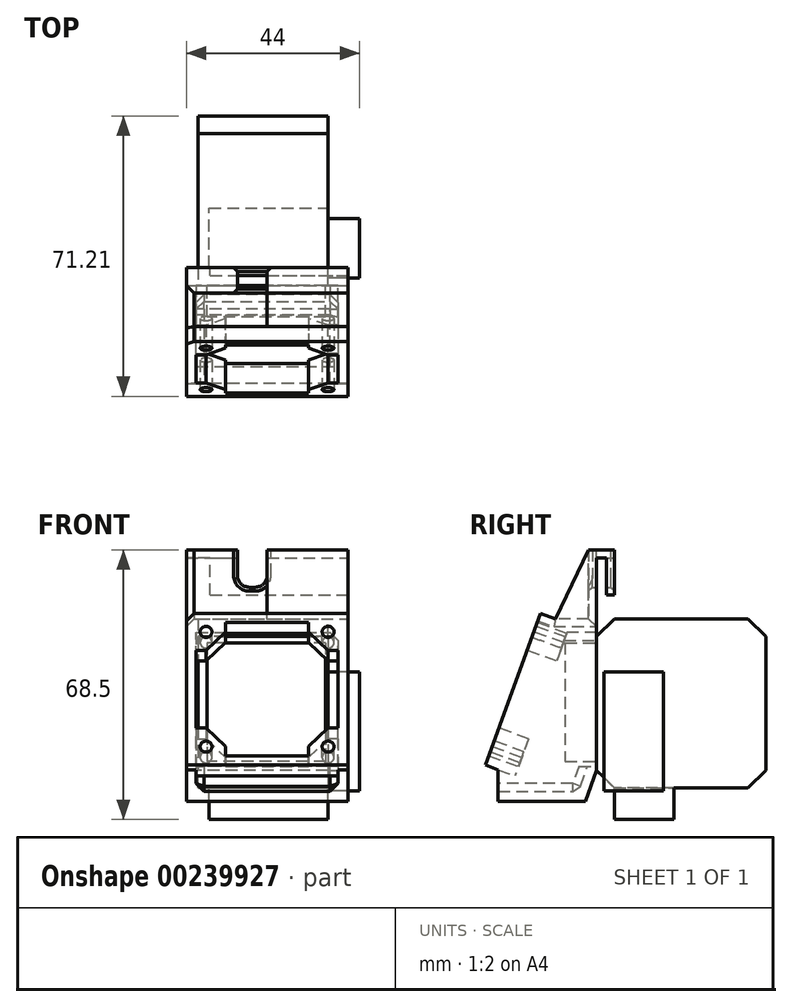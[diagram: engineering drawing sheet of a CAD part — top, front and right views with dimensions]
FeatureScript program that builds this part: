
annotation { "Feature Type Name" : "Feature", "Feature Type Description" : "" }
export const myFeature = defineFeature(function(context is Context, id is Id, definition is map)
    precondition{}
    {
        {
            var Q0;
            Q0=qCreatedBy(makeId("Front.planeOp"),FACE);
            var sketch = newSketch(context, id + "F0", { "sketchPlane" : qUnion([Q0])});
            skLineSegment(sketch, "E0.bottom", {"start": v(0, 0) * mm, "end": v(-33, 0) * mm});
            skLineSegment(sketch, "E0.top", {"start": v(0, -43) * mm, "end": v(-33, -43) * mm});
            skLineSegment(sketch, "E0.left", {"start": v(0, 0) * mm, "end": v(0, -43) * mm});
            skLineSegment(sketch, "E0.right", {"start": v(-33, 0) * mm, "end": v(-33, -43) * mm});
            skSolve(sketch);
        }
        {
            var Q0;
            Q0=makeQuery(id+"F0.imprint","IMPRINT",FACE,{"disambiguationData":[TD([[makeQuery(id+"F0.imprint","IMPRINT",EDGE,{"derivedFrom":sQuery(id+"F0.wireOp",EDGE,"E0.bottom")}),1.0]])]});
            extrude(context, id + "F1", {"entities" : qUnion([Q0]), "oppositeDirection" : true, "depth" : 43 * mm, "offsetDistance" : 25 * mm});
        }
        {
            var Q0;
            Q0=makeQuery(id+"F1.opExtrude","CAP_EDGE",EDGE,{"disambiguationData":[OSD([sQuery(id+"F0.wireOp",EDGE,"E0.bottom")])],"isStart":true});
            var Q1;
            Q1=makeQuery(id+"F1.opExtrude","CAP_EDGE",EDGE,{"disambiguationData":[OSD([sQuery(id+"F0.wireOp",EDGE,"E0.bottom")])],"isStart":false});
            var Q2;
            Q2=makeQuery(id+"F1.opExtrude","CAP_EDGE",EDGE,{"disambiguationData":[OSD([sQuery(id+"F0.wireOp",EDGE,"E0.top")])],"isStart":true});
            var Q3;
            Q3=makeQuery(id+"F1.opExtrude","CAP_EDGE",EDGE,{"disambiguationData":[OSD([sQuery(id+"F0.wireOp",EDGE,"E0.top")])],"isStart":false});
            chamfer(context, id + "F2", {"entities" : qUnion([Q0, Q1, Q2, Q3]), "width" : 4.5 * mm, "tangentPropagation" : true});
        }
        {
            var Q0;
            Q0=makeQuery(id+"F1.opExtrude","CAP_FACE",FACE,{"disambiguationData":[OSD([sQuery(id+"F0.wireOp",EDGE,"E0.bottom"),sQuery(id+"F0.wireOp",EDGE,"E0.top"),sQuery(id+"F0.wireOp",EDGE,"E0.left"),sQuery(id+"F0.wireOp",EDGE,"E0.right")])],"isStart":true});
            var sketch = newSketch(context, id + "F3", { "sketchPlane" : qUnion([Q0])});
            skLineSegment(sketch, "E1.bottom", {"start": v(-0.6, -6.1) * mm, "end": v(-30.8, -6.1) * mm});
            skLineSegment(sketch, "E1.top", {"start": v(-0.6, -36.3) * mm, "end": v(-30.8, -36.3) * mm});
            skLineSegment(sketch, "E1.left", {"start": v(-0.6, -6.1) * mm, "end": v(-0.6, -36.3) * mm});
            skLineSegment(sketch, "E1.right", {"start": v(-30.8, -6.1) * mm, "end": v(-30.8, -36.3) * mm});
            skSolve(sketch);
        }
        {
            var Q0;
            Q0 = qSketchRegion(id + "F3", true);
            extrude(context, id + "F4", {"entities" : qUnion([Q0]), "operationType" : NewBodyOperationType.ADD, "depth" : 8 * mm, "offsetDistance" : 25 * mm});
        }
        {
            var Q0;
            Q0=makeQuery(id+"F1.opExtrude","SWEPT_FACE",FACE,{"disambiguationData":[OSD([sQuery(id+"F0.wireOp",EDGE,"E0.top")])]});
            var sketch = newSketch(context, id + "F5", { "sketchPlane" : qUnion([Q0])});
            skLineSegment(sketch, "E2.bottom", {"start": v(-30.2, -4.5) * mm, "end": v(0, -4.5) * mm});
            skLineSegment(sketch, "E2.top", {"start": v(-30.2, -19.6) * mm, "end": v(0, -19.6) * mm});
            skLineSegment(sketch, "E2.left", {"start": v(-30.2, -4.5) * mm, "end": v(-30.2, -19.6) * mm});
            skLineSegment(sketch, "E2.right", {"start": v(0, -4.5) * mm, "end": v(0, -19.6) * mm});
            skSolve(sketch);
        }
        {
            var Q0;
            Q0 = qSketchRegion(id + "F5", true);
            extrude(context, id + "F6", {"entities" : qUnion([Q0]), "operationType" : NewBodyOperationType.ADD, "depth" : 8 * mm, "offsetDistance" : 25 * mm});
        }
        {
            var Q0;
            Q0=makeQuery(id+"F6.boolean.opBoolean","MERGE",FACE,{"derivedFrom":[makeQuery(id+"F1.opExtrude","SWEPT_FACE",FACE,{"disambiguationData":[OSD([sQuery(id+"F0.wireOp",EDGE,"E0.left")])]}),makeQuery(id+"F6.opExtrude","SWEPT_FACE",FACE,{"disambiguationData":[OSD([sQuery(id+"F5.wireOp",EDGE,"E2.right")])]})]});
            var sketch = newSketch(context, id + "F7", { "sketchPlane" : qUnion([Q0])});
            skLineSegment(sketch, "E3.bottom", {"start": v(1.85, -13.5) * mm, "end": v(16.95, -13.5) * mm});
            skLineSegment(sketch, "E3.top", {"start": v(1.85, -43.7) * mm, "end": v(16.95, -43.7) * mm});
            skLineSegment(sketch, "E3.left", {"start": v(1.85, -13.5) * mm, "end": v(1.85, -43.7) * mm});
            skLineSegment(sketch, "E3.right", {"start": v(16.95, -13.5) * mm, "end": v(16.95, -43.7) * mm});
            skSolve(sketch);
        }
        {
            var Q0;
            Q0 = qSketchRegion(id + "F7", true);
            extrude(context, id + "F8", {"entities" : qUnion([Q0]), "operationType" : NewBodyOperationType.ADD, "depth" : 8 * mm, "offsetDistance" : 25 * mm});
        }
        {
            var Q0;
            Q0=qCreatedBy(makeId("Right.planeOp"),FACE);
            cPlane(context, id + "F9", {"entities" : qUnion([Q0]), "cplaneType" : CPlaneType.OFFSET, "offset" : 5 * mm, "width" : 150 * mm, "height" : 150 * mm});
        }
        {
            var Q0;
            Q0=qCreatedBy(id+"F9.planeOp",FACE);
            var sketch = newSketch(context, id + "F10", { "sketchPlane" : qUnion([Q0])});
            skLineSegment(sketch, "E4", {"start": v(-2, -3.5) * mm, "end": v(-2, 17.5) * mm});
            skLineSegment(sketch, "E5", {"start": v(-2, 17.5) * mm, "end": v(4.5, 17.5) * mm});
            skLineSegment(sketch, "E6", {"start": v(4.5, 17.5) * mm, "end": v(4.5, 6) * mm});
            skLineSegment(sketch, "E7", {"start": v(4.5, 6) * mm, "end": v(2.5, 6) * mm});
            skLineSegment(sketch, "E8", {"start": v(2.5, 6) * mm, "end": v(2.5, 15.5) * mm});
            skLineSegment(sketch, "E9", {"start": v(2.5, 15.5) * mm, "end": v(0, 15.5) * mm});
            skLineSegment(sketch, "E10", {"start": v(0, 15.5) * mm, "end": v(0, -3.5) * mm});
            skLineSegment(sketch, "E11", {"start": v(0, -3.5) * mm, "end": v(-2, -3.5) * mm});
            skSolve(sketch);
        }
        {
            var Q0;
            Q0 = qSketchRegion(id + "F10", true);
            extrude(context, id + "F11", {"entities" : qUnion([Q0]), "oppositeDirection" : true, "depth" : 35 * mm, "offsetDistance" : 25 * mm});
        }
        {
            var Q0;
            Q0=makeQuery(id+"F11.opExtrude","SWEPT_FACE",FACE,{"disambiguationData":[OSD([sQuery(id+"F10.wireOp",EDGE,"E4")])]});
            var sketch = newSketch(context, id + "F12", { "sketchPlane" : qUnion([Q0])});
            skLineSegment(sketch, "E12", {"start": v(-15.5, 8) * mm, "end": v(-15.5, 17.5) * mm});
            skLineSegment(sketch, "E13", {"start": v(-15.5, 8) * mm, "end": v(-23, 8) * mm});
            skLineSegment(sketch, "E14", {"start": v(-23, 17.5) * mm, "end": v(-23, 8) * mm});
            skLineSegment(sketch, "E15", {"start": v(-23, 17.5) * mm, "end": v(-15.5, 17.5) * mm});
            skSolve(sketch);
        }
        {
            var Q0;
            Q0 = qSketchRegion(id + "F12", true);
            var Q1;
            Q1=makeQuery(id+"F11.opExtrude","SWEPT_FACE",FACE,{"disambiguationData":[OSD([sQuery(id+"F10.wireOp",EDGE,"E6")])]});
            extrude(context, id + "F13", {"entities" : qUnion([Q0]), "operationType" : NewBodyOperationType.REMOVE, "endBound" : BoundingType.SYMMETRIC, "depth" : 50 * mm, "endBoundEntityFace" : qUnion([Q1]), "offsetDistance" : 25 * mm});
        }
        {
            var Q0;
            {var subQ0=sQuery(id+"F12.wireOp",EDGE,"E13");var subQ1=sQuery(id+"F12.wireOp",EDGE,"E12");Q0=makeQuery(id+"F13.boolean.opBoolean","COPY",EDGE,{"disambiguationData":[TD([makeQuery(id+"F11.opExtrude","SWEPT_FACE",FACE,{"disambiguationData":[OSD([sQuery(id+"F10.wireOp",EDGE,"E6")])]})])],"derivedFrom":makeQuery(id+"F13.opExtrude","SWEPT_EDGE",EDGE,{"disambiguationData":[OSD([subQ1,subQ0])]})});}
            var Q1;
            {var subQ0=sQuery(id+"F12.wireOp",EDGE,"E12");var subQ1=sQuery(id+"F12.wireOp",EDGE,"E13");Q1=makeQuery(id+"F13.boolean.opBoolean","COPY",EDGE,{"disambiguationData":[TD([makeQuery(id+"F11.opExtrude","SWEPT_FACE",FACE,{"disambiguationData":[OSD([sQuery(id+"F10.wireOp",EDGE,"E4")])]})])],"derivedFrom":makeQuery(id+"F13.opExtrude","SWEPT_EDGE",EDGE,{"disambiguationData":[OSD([subQ0,subQ1])]})});}
            var Q2;
            {var subQ0=sQuery(id+"F12.wireOp",EDGE,"E13");var subQ1=sQuery(id+"F12.wireOp",EDGE,"E14");Q2=makeQuery(id+"F13.boolean.opBoolean","COPY",EDGE,{"disambiguationData":[TD([makeQuery(id+"F11.opExtrude","SWEPT_FACE",FACE,{"disambiguationData":[OSD([sQuery(id+"F10.wireOp",EDGE,"E6")])]})])],"derivedFrom":makeQuery(id+"F13.opExtrude","SWEPT_EDGE",EDGE,{"disambiguationData":[OSD([subQ0,subQ1])]})});}
            var Q3;
            {var subQ0=sQuery(id+"F12.wireOp",EDGE,"E13");var subQ1=sQuery(id+"F12.wireOp",EDGE,"E14");Q3=makeQuery(id+"F13.boolean.opBoolean","COPY",EDGE,{"disambiguationData":[TD([makeQuery(id+"F11.opExtrude","SWEPT_FACE",FACE,{"disambiguationData":[OSD([sQuery(id+"F10.wireOp",EDGE,"E4")])]})])],"derivedFrom":makeQuery(id+"F13.opExtrude","SWEPT_EDGE",EDGE,{"disambiguationData":[OSD([subQ0,subQ1])]})});}
            fillet(context, id + "F14", {"entities" : qUnion([Q0, Q1, Q2, Q3]), "radius" : 3 * mm, "tangentPropagation" : true, "allowEdgeOverflow" : false});
        }
        {
            var Q0;
            Q0=qCreatedBy(id+"F9.planeOp",FACE);
            var sketch = newSketch(context, id + "F15", { "sketchPlane" : qUnion([Q0])});
            skLineSegment(sketch, "E16", {"start": v(-10.5, 0) * mm, "end": v(-24.45, -38.55) * mm});
            skLineSegment(sketch, "E17", {"start": v(-24.45, -38.55) * mm, "end": v(-2.85, -46.37) * mm});
            skLineSegment(sketch, "E18", {"start": v(-10.5, 0) * mm, "end": v(-2, 17.5) * mm});
            skPoint(sketch, "E19.orphan", {"position": v(19.6, 0) * mm});
            skLineSegment(sketch, "E20", {"start": v(0, -38.5) * mm, "end": v(0, 17.5) * mm});
            skLineSegment(sketch, "E21", {"start": v(0, 17.5) * mm, "end": v(-2, 17.5) * mm});
            skLineSegment(sketch, "E22", {"start": v(-2.85, -46.37) * mm, "end": v(0, -38.5) * mm});
            skLineSegment(sketch, "E23", {"start": v(-2.85, -46.37) * mm, "end": v(0, -47.4) * mm, "construction": true});
            skLineSegment(sketch, "E24", {"start": v(0, -47.4) * mm, "end": v(0, -38.5) * mm, "construction": true});
            skSolve(sketch);
        }
        {
            var Q0;
            Q0 = qSketchRegion(id + "F15", true);
            var Q1;
            Q1=makeQuery(id+"F6.boolean.opBoolean","MERGE",FACE,{"derivedFrom":[makeQuery(id+"F1.opExtrude","SWEPT_FACE",FACE,{"disambiguationData":[OSD([sQuery(id+"F0.wireOp",EDGE,"E0.left")])]}),makeQuery(id+"F6.opExtrude","SWEPT_FACE",FACE,{"disambiguationData":[OSD([sQuery(id+"F5.wireOp",EDGE,"E2.right")])]})]});
            extrude(context, id + "F16", {"entities" : qUnion([Q0]), "operationType" : NewBodyOperationType.ADD, "oppositeDirection" : true, "depth" : 2.5 * mm, "endBoundEntityFace" : qUnion([Q1]), "offsetDistance" : 25 * mm});
        }
        {
            var Q0;
            Q0=qCreatedBy(id+"F9.planeOp",FACE);
            var sketch = newSketch(context, id + "F17", { "sketchPlane" : qUnion([Q0])});
            skLineSegment(sketch, "E25", {"start": v(0, -3.5) * mm, "end": v(-8.17, -3.5) * mm});
            skLineSegment(sketch, "E26", {"start": v(-11.77, -3.5) * mm, "end": v(-11.35, -2.35) * mm, "construction": true});
            skLineSegment(sketch, "E27", {"start": v(-10.5, 0) * mm, "end": v(-2, 17.5) * mm});
            skLineSegment(sketch, "E28", {"start": v(-2, 17.5) * mm, "end": v(0, 17.5) * mm});
            skLineSegment(sketch, "E29", {"start": v(0, 17.5) * mm, "end": v(0, -3.5) * mm});
            skLineSegment(sketch, "E30", {"start": v(0, 17.5) * mm, "end": v(4.5, 17.5) * mm});
            skLineSegment(sketch, "E31", {"start": v(4.5, 17.5) * mm, "end": v(4.5, 15.5) * mm});
            skLineSegment(sketch, "E32", {"start": v(4.5, 15.5) * mm, "end": v(0, 15.5) * mm});
            skLineSegment(sketch, "E33", {"start": v(-11.35, -2.35) * mm, "end": v(-10.5, 0) * mm});
            skLineSegment(sketch, "E34", {"start": v(-11.35, -2.35) * mm, "end": v(-8.17, -3.5) * mm});
            skSolve(sketch);
        }
        {
            var Q0;
            Q0=makeQuery(id+"F16.opExtrude","SWEPT_FACE",FACE,{"disambiguationData":[OSD([sQuery(id+"F15.wireOp",EDGE,"E16")])]});
            var sketch = newSketch(context, id + "F18", { "sketchPlane" : qUnion([Q0])});
            skLineSegment(sketch, "E35", {"start": v(5, -3.57) * mm, "end": v(-36, -3.57) * mm});
            skLineSegment(sketch, "E36", {"start": v(-36, -3.57) * mm, "end": v(-36, -44.57) * mm});
            skLineSegment(sketch, "E37", {"start": v(-36, -44.57) * mm, "end": v(5, -44.57) * mm});
            skLineSegment(sketch, "E38", {"start": v(5, -44.57) * mm, "end": v(5, -3.57) * mm});
            skLineSegment(sketch, "E39.bottom", {"start": v(-33.5, -6.07) * mm, "end": v(2.5, -6.07) * mm});
            skLineSegment(sketch, "E39.top", {"start": v(-33.5, -42.07) * mm, "end": v(2.5, -42.07) * mm});
            skLineSegment(sketch, "E39.left", {"start": v(-33.5, -6.07) * mm, "end": v(-33.5, -42.07) * mm});
            skLineSegment(sketch, "E39.right", {"start": v(2.5, -6.07) * mm, "end": v(2.5, -42.07) * mm});
            skSolve(sketch);
        }
        {
            var Q0;
            Q0 = qSketchRegion(id + "F18", true);
            extrude(context, id + "F19", {"entities" : qUnion([Q0]), "operationType" : NewBodyOperationType.ADD, "endBound" : BoundingType.SYMMETRIC, "depth" : 8 * mm, "offsetDistance" : 25 * mm});
        }
        {
            var Q0;
            Q0 = qSketchRegion(id + "F17", true);
            var Q1;
            Q1=makeQuery(id+"F13.boolean.opBoolean","COPY",FACE,{"derivedFrom":makeQuery(id+"F13.opExtrude","SWEPT_FACE",FACE,{"disambiguationData":[OSD([sQuery(id+"F12.wireOp",EDGE,"E12")])]})});
            extrude(context, id + "F20", {"entities" : qUnion([Q0]), "operationType" : NewBodyOperationType.ADD, "endBound" : BoundingType.UP_TO_SURFACE, "oppositeDirection" : true, "depth" : 25 * mm, "endBoundEntityFace" : qUnion([Q1]), "offsetDistance" : 25 * mm});
        }
        {
            var Q0;
            Q0=makeQuery(id+"F19.opExtrude","SWEPT_FACE",FACE,{"disambiguationData":[OSD([sQuery(id+"F18.wireOp",EDGE,"E36")])]});
            var sketch = newSketch(context, id + "F21", { "sketchPlane" : qUnion([Q0])});
            skLineSegment(sketch, "E40", {"start": v(0, -3.5) * mm, "end": v(7.51, -3.5) * mm});
            skLineSegment(sketch, "E41", {"start": v(7.51, -3.5) * mm, "end": v(11.27, -2.14) * mm});
            skLineSegment(sketch, "E42", {"start": v(11.27, -2.14) * mm, "end": v(10.5, 0) * mm});
            skLineSegment(sketch, "E43", {"start": v(10.5, 0) * mm, "end": v(0, 0) * mm});
            skLineSegment(sketch, "E44", {"start": v(0, 0) * mm, "end": v(0, -3.5) * mm});
            skSolve(sketch);
        }
        {
            var Q0;
            Q0 = qSketchRegion(id + "F21", true);
            var Q1;
            {var subQ0=sQuery(id+"F12.wireOp",EDGE,"E12");Q1=makeQuery(id+"F20.boolean.opBoolean","MERGE",FACE,{"derivedFrom":[makeQuery(id+"F13.boolean.opBoolean","COPY",FACE,{"derivedFrom":makeQuery(id+"F13.opExtrude","SWEPT_FACE",FACE,{"disambiguationData":[OSD([subQ0])]})}),makeQuery(id+"F20.opExtrude","CAP_FACE",FACE,{"disambiguationData":[OSD([subQ0])],"isStart":false})]});}
            extrude(context, id + "F22", {"entities" : qUnion([Q0]), "operationType" : NewBodyOperationType.ADD, "endBound" : BoundingType.UP_TO_SURFACE, "oppositeDirection" : true, "depth" : 25 * mm, "endBoundEntityFace" : qUnion([Q1]), "offsetDistance" : 25 * mm});
        }
        {
            var Q0;
            Q0=makeQuery(id+"F22.boolean.opBoolean","MERGE",FACE,{"derivedFrom":[makeQuery(id+"F19.opExtrude","SWEPT_FACE",FACE,{"disambiguationData":[OSD([sQuery(id+"F18.wireOp",EDGE,"E36")])]}),makeQuery(id+"F22.opExtrude","CAP_FACE",FACE,{"disambiguationData":[OSD([sQuery(id+"F21.wireOp",EDGE,"E40"),sQuery(id+"F21.wireOp",EDGE,"E41"),sQuery(id+"F21.wireOp",EDGE,"E42"),sQuery(id+"F21.wireOp",EDGE,"E43"),sQuery(id+"F21.wireOp",EDGE,"E44")])],"isStart":true})]});
            var sketch = newSketch(context, id + "F23", { "sketchPlane" : qUnion([Q0])});
            skLineSegment(sketch, "E45.bottom", {"start": v(2, -3.5) * mm, "end": v(0, -3.5) * mm});
            skLineSegment(sketch, "E45.top", {"start": v(2, 17.5) * mm, "end": v(0, 17.5) * mm});
            skLineSegment(sketch, "E45.left", {"start": v(2, -3.5) * mm, "end": v(2, 17.5) * mm});
            skLineSegment(sketch, "E45.right", {"start": v(0, -3.5) * mm, "end": v(0, 17.5) * mm});
            skLineSegment(sketch, "E46.bottom", {"start": v(0, 17.5) * mm, "end": v(-4.5, 17.5) * mm});
            skLineSegment(sketch, "E46.top", {"start": v(0, 15.5) * mm, "end": v(-4.5, 15.5) * mm});
            skLineSegment(sketch, "E46.left", {"start": v(0, 17.5) * mm, "end": v(0, 15.5) * mm});
            skLineSegment(sketch, "E46.right", {"start": v(-4.5, 17.5) * mm, "end": v(-4.5, 15.5) * mm});
            skSolve(sketch);
        }
        {
            var Q0;
            Q0 = qSketchRegion(id + "F23", true);
            var Q1;
            Q1=makeQuery(id+"F11.opExtrude","CAP_FACE",FACE,{"disambiguationData":[OSD([sQuery(id+"F10.wireOp",EDGE,"E4"),sQuery(id+"F10.wireOp",EDGE,"E5"),sQuery(id+"F10.wireOp",EDGE,"E6"),sQuery(id+"F10.wireOp",EDGE,"E7"),sQuery(id+"F10.wireOp",EDGE,"E8"),sQuery(id+"F10.wireOp",EDGE,"E9"),sQuery(id+"F10.wireOp",EDGE,"E10"),sQuery(id+"F10.wireOp",EDGE,"E11")])],"isStart":false});
            extrude(context, id + "F24", {"entities" : qUnion([Q0]), "operationType" : NewBodyOperationType.ADD, "endBound" : BoundingType.UP_TO_SURFACE, "oppositeDirection" : true, "depth" : 25 * mm, "endBoundEntityFace" : qUnion([Q1]), "offsetDistance" : 25 * mm});
        }
        {
            var Q0;
            Q0=makeQuery(id+"F34.opChamfer","SPLIT",FACE,{"disambiguationData":[OD(0.0)],"derivedFrom":makeQuery(id+"F24.boolean.opBoolean","MERGE",FACE,{"derivedFrom":[makeQuery(id+"F22.boolean.opBoolean","MERGE",FACE,{"derivedFrom":[makeQuery(id+"F19.opExtrude","SWEPT_FACE",FACE,{"disambiguationData":[OSD([sQuery(id+"F18.wireOp",EDGE,"E36")])]}),makeQuery(id+"F22.opExtrude","CAP_FACE",FACE,{"disambiguationData":[OSD([sQuery(id+"F21.wireOp",EDGE,"E40"),sQuery(id+"F21.wireOp",EDGE,"E41"),sQuery(id+"F21.wireOp",EDGE,"E42"),sQuery(id+"F21.wireOp",EDGE,"E43"),sQuery(id+"F21.wireOp",EDGE,"E44")])],"isStart":true})]}),makeQuery(id+"F24.opExtrude","CAP_FACE",FACE,{"disambiguationData":[OSD([sQuery(id+"F23.wireOp",EDGE,"E45.bottom"),sQuery(id+"F23.wireOp",EDGE,"E45.top"),sQuery(id+"F23.wireOp",EDGE,"E45.left"),sQuery(id+"F23.wireOp",EDGE,"E45.right"),sQuery(id+"F23.wireOp",EDGE,"E46.bottom"),sQuery(id+"F23.wireOp",EDGE,"E46.top"),sQuery(id+"F23.wireOp",EDGE,"E46.right")])],"isStart":true})]})});
            var sketch = newSketch(context, id + "F25", { "sketchPlane" : qUnion([Q0])});
            skLineSegment(sketch, "E47", {"start": v(0, -38.5) * mm, "end": v(0, -3.5) * mm});
            skLineSegment(sketch, "E48", {"start": v(0, -3.5) * mm, "end": v(11.77, -3.5) * mm});
            skLineSegment(sketch, "E49", {"start": v(11.77, -3.5) * mm, "end": v(24.45, -38.55) * mm});
            skLineSegment(sketch, "E50", {"start": v(24.45, -38.55) * mm, "end": v(0, -38.5) * mm});
            skLineSegment(sketch, "E51", {"start": v(0, -38.5) * mm, "end": v(2.85, -46.37) * mm});
            skLineSegment(sketch, "E52", {"start": v(2.85, -46.37) * mm, "end": v(24.45, -38.55) * mm});
            skSolve(sketch);
        }
        {
            var Q0;
            Q0 = qSketchRegion(id + "F25", true);
            extrude(context, id + "F26", {"entities" : qUnion([Q0]), "operationType" : NewBodyOperationType.ADD, "oppositeDirection" : true, "depth" : 2.5 * mm, "offsetDistance" : 25 * mm});
        }
        {
            var Q0;
            Q0=makeQuery(id+"F26.boolean.opBoolean","MERGE",FACE,{"derivedFrom":[makeQuery(id+"F34.opChamfer","SPLIT",FACE,{"disambiguationData":[OD(0.0)],"derivedFrom":makeQuery(id+"F24.boolean.opBoolean","MERGE",FACE,{"derivedFrom":[makeQuery(id+"F22.boolean.opBoolean","MERGE",FACE,{"derivedFrom":[makeQuery(id+"F19.opExtrude","SWEPT_FACE",FACE,{"disambiguationData":[OSD([sQuery(id+"F18.wireOp",EDGE,"E36")])]}),makeQuery(id+"F22.opExtrude","CAP_FACE",FACE,{"disambiguationData":[OSD([sQuery(id+"F21.wireOp",EDGE,"E40"),sQuery(id+"F21.wireOp",EDGE,"E41"),sQuery(id+"F21.wireOp",EDGE,"E42"),sQuery(id+"F21.wireOp",EDGE,"E43"),sQuery(id+"F21.wireOp",EDGE,"E44")])],"isStart":true})]}),makeQuery(id+"F24.opExtrude","CAP_FACE",FACE,{"disambiguationData":[OSD([sQuery(id+"F23.wireOp",EDGE,"E45.bottom"),sQuery(id+"F23.wireOp",EDGE,"E45.top"),sQuery(id+"F23.wireOp",EDGE,"E45.left"),sQuery(id+"F23.wireOp",EDGE,"E45.right"),sQuery(id+"F23.wireOp",EDGE,"E46.bottom"),sQuery(id+"F23.wireOp",EDGE,"E46.top"),sQuery(id+"F23.wireOp",EDGE,"E46.right")])],"isStart":true})]})}),makeQuery(id+"F26.opExtrude","CAP_FACE",FACE,{"disambiguationData":[OSD([sQuery(id+"F25.wireOp",EDGE,"E47"),sQuery(id+"F25.wireOp",EDGE,"E48"),sQuery(id+"F25.wireOp",EDGE,"E49"),sQuery(id+"F25.wireOp",EDGE,"E50")])],"isStart":true})]});
            var sketch = newSketch(context, id + "F27", { "sketchPlane" : qUnion([Q0])});
            skLineSegment(sketch, "E53", {"start": v(2.85, -46.37) * mm, "end": v(25, -46.37) * mm});
            skLineSegment(sketch, "E54", {"start": v(25, -46.37) * mm, "end": v(25, -43.87) * mm});
            skLineSegment(sketch, "E55", {"start": v(25, -43.87) * mm, "end": v(1.94, -43.87) * mm});
            skLineSegment(sketch, "E56", {"start": v(1.94, -43.87) * mm, "end": v(2.85, -46.37) * mm});
            skLineSegment(sketch, "E57", {"start": v(1.94, -43.87) * mm, "end": v(0, -38.5) * mm});
            skLineSegment(sketch, "E58", {"start": v(0, -38.5) * mm, "end": v(0, -37.5) * mm});
            skLineSegment(sketch, "E59", {"start": v(0, -37.5) * mm, "end": v(2.3, -37.5) * mm});
            skLineSegment(sketch, "E60", {"start": v(2.3, -37.5) * mm, "end": v(4.6, -43.87) * mm});
            skSolve(sketch);
        }
        {
            var Q0;
            Q0 = qSketchRegion(id + "F27", true);
            var Q1;
            Q1=makeQuery(id+"F19.boolean.opBoolean","MERGE",FACE,{"derivedFrom":[makeQuery(id+"F16.boolean.opBoolean","MERGE",FACE,{"derivedFrom":[makeQuery(id+"F11.opExtrude","CAP_FACE",FACE,{"disambiguationData":[OSD([sQuery(id+"F10.wireOp",EDGE,"E4"),sQuery(id+"F10.wireOp",EDGE,"E5"),sQuery(id+"F10.wireOp",EDGE,"E6"),sQuery(id+"F10.wireOp",EDGE,"E7"),sQuery(id+"F10.wireOp",EDGE,"E8"),sQuery(id+"F10.wireOp",EDGE,"E9"),sQuery(id+"F10.wireOp",EDGE,"E10"),sQuery(id+"F10.wireOp",EDGE,"E11")])],"isStart":true}),makeQuery(id+"F16.opExtrude","CAP_FACE",FACE,{"disambiguationData":[OSD([sQuery(id+"F15.wireOp",EDGE,"E16"),sQuery(id+"F15.wireOp",EDGE,"E17"),sQuery(id+"F15.wireOp",EDGE,"E18"),sQuery(id+"F15.wireOp",EDGE,"E20"),sQuery(id+"F15.wireOp",EDGE,"E21")])],"isStart":true})]}),makeQuery(id+"F19.opExtrude","SWEPT_FACE",FACE,{"disambiguationData":[OSD([sQuery(id+"F18.wireOp",EDGE,"E38")])]})]});
            extrude(context, id + "F28", {"entities" : qUnion([Q0]), "operationType" : NewBodyOperationType.ADD, "endBound" : BoundingType.UP_TO_SURFACE, "oppositeDirection" : true, "depth" : 25 * mm, "endBoundEntityFace" : qUnion([Q1]), "offsetDistance" : 25 * mm});
        }
        {
            var Q0;
            Q0=makeQuery(id+"F28.opExtrude","SWEPT_FACE",FACE,{"disambiguationData":[OSD([sQuery(id+"F27.wireOp",EDGE,"E54")])]});
            var sketch = newSketch(context, id + "F29", { "sketchPlane" : qUnion([Q0])});
            skLineSegment(sketch, "E61.bottom", {"start": v(-36, -46.37) * mm, "end": v(-33.5, -46.37) * mm});
            skLineSegment(sketch, "E61.top", {"start": v(-36, -37.2) * mm, "end": v(-33.5, -37.2) * mm});
            skLineSegment(sketch, "E61.left", {"start": v(-36, -46.37) * mm, "end": v(-36, -37.2) * mm});
            skLineSegment(sketch, "E61.right", {"start": v(-33.5, -46.37) * mm, "end": v(-33.5, -37.2) * mm});
            skLineSegment(sketch, "E62.bottom", {"start": v(5, -46.37) * mm, "end": v(2.5, -46.37) * mm});
            skLineSegment(sketch, "E62.top", {"start": v(5, -37.2) * mm, "end": v(2.5, -37.2) * mm});
            skLineSegment(sketch, "E62.left", {"start": v(5, -46.37) * mm, "end": v(5, -37.2) * mm});
            skLineSegment(sketch, "E62.right", {"start": v(2.5, -46.37) * mm, "end": v(2.5, -37.2) * mm});
            skSolve(sketch);
        }
        {
            var Q0;
            Q0 = qSketchRegion(id + "F29", true);
            var Q1;
            Q1=makeQuery(id+"F26.boolean.opBoolean","MERGE",FACE,{"derivedFrom":[makeQuery(id+"F19.boolean.opBoolean","MERGE",FACE,{"derivedFrom":[makeQuery(id+"F16.opExtrude","SWEPT_FACE",FACE,{"disambiguationData":[OSD([sQuery(id+"F15.wireOp",EDGE,"E17")])]}),makeQuery(id+"F19.opExtrude","SWEPT_FACE",FACE,{"disambiguationData":[OSD([sQuery(id+"F18.wireOp",EDGE,"E37")])]})]}),makeQuery(id+"F26.opExtrude","SWEPT_FACE",FACE,{"disambiguationData":[OSD([sQuery(id+"F25.wireOp",EDGE,"E52")])]})]});
            var Q2;
            Q2=makeQuery(id+"F28.boolean.opBoolean","MERGE",FACE,{"derivedFrom":[makeQuery(id+"F26.boolean.opBoolean","MERGE",FACE,{"derivedFrom":[makeQuery(id+"F24.boolean.opBoolean","MERGE",FACE,{"derivedFrom":[makeQuery(id+"F22.boolean.opBoolean","MERGE",FACE,{"derivedFrom":[makeQuery(id+"F16.boolean.opBoolean","MERGE",FACE,{"derivedFrom":[makeQuery(id+"F11.opExtrude","SWEPT_FACE",FACE,{"disambiguationData":[OSD([sQuery(id+"F10.wireOp",EDGE,"E10")])]}),makeQuery(id+"F16.opExtrude","SWEPT_FACE",FACE,{"disambiguationData":[OSD([sQuery(id+"F15.wireOp",EDGE,"E20")])]})]}),makeQuery(id+"F22.opExtrude","SWEPT_FACE",FACE,{"disambiguationData":[OSD([sQuery(id+"F21.wireOp",EDGE,"E44")])]})]}),makeQuery(id+"F24.opExtrude","SWEPT_FACE",FACE,{"disambiguationData":[OSD([sQuery(id+"F23.wireOp",EDGE,"E45.right")])]})]}),makeQuery(id+"F26.opExtrude","SWEPT_FACE",FACE,{"disambiguationData":[OSD([sQuery(id+"F25.wireOp",EDGE,"E47")])]})]}),makeQuery(id+"F28.opExtrude","SWEPT_FACE",FACE,{"disambiguationData":[OSD([sQuery(id+"F27.wireOp",EDGE,"E58")])]})]});
            extrude(context, id + "F30", {"entities" : qUnion([Q0]), "operationType" : NewBodyOperationType.ADD, "endBound" : BoundingType.UP_TO_SURFACE, "oppositeDirection" : true, "depth" : 25 * mm, "endBoundEntityFace" : qUnion([Q1]), "offsetDistance" : 25 * mm});
        }
        {
            var Q0;
            Q0=makeQuery(id+"F19.opExtrude","CAP_FACE",FACE,{"disambiguationData":[OSD([sQuery(id+"F18.wireOp",EDGE,"E35"),sQuery(id+"F18.wireOp",EDGE,"E36"),sQuery(id+"F18.wireOp",EDGE,"E37"),sQuery(id+"F18.wireOp",EDGE,"E38"),sQuery(id+"F18.wireOp",EDGE,"E39.bottom"),sQuery(id+"F18.wireOp",EDGE,"E39.top"),sQuery(id+"F18.wireOp",EDGE,"E39.left"),sQuery(id+"F18.wireOp",EDGE,"E39.right")])],"isStart":false});
            var sketch = newSketch(context, id + "F31", { "sketchPlane" : qUnion([Q0])});
            skLineSegment(sketch, "E63.bottom", {"start": v(5, -44.57) * mm, "end": v(-5, -44.57) * mm});
            skLineSegment(sketch, "E63.top", {"start": v(5, -34.57) * mm, "end": v(-5, -34.57) * mm});
            skLineSegment(sketch, "E63.left", {"start": v(5, -44.57) * mm, "end": v(5, -34.57) * mm});
            skLineSegment(sketch, "E63.right", {"start": v(-5, -44.57) * mm, "end": v(-5, -34.57) * mm});
            skLineSegment(sketch, "E64.bottom", {"start": v(-36, -44.57) * mm, "end": v(-26, -44.57) * mm});
            skLineSegment(sketch, "E64.top", {"start": v(-36, -34.57) * mm, "end": v(-26, -34.57) * mm});
            skLineSegment(sketch, "E64.left", {"start": v(-36, -44.57) * mm, "end": v(-36, -34.57) * mm});
            skLineSegment(sketch, "E64.right", {"start": v(-26, -44.57) * mm, "end": v(-26, -34.57) * mm});
            skLineSegment(sketch, "E65.bottom", {"start": v(5, -3.57) * mm, "end": v(-5, -3.57) * mm});
            skLineSegment(sketch, "E65.top", {"start": v(5, -13.57) * mm, "end": v(-5, -13.57) * mm});
            skLineSegment(sketch, "E65.left", {"start": v(5, -3.57) * mm, "end": v(5, -13.57) * mm});
            skLineSegment(sketch, "E65.right", {"start": v(-5, -3.57) * mm, "end": v(-5, -13.57) * mm});
            skLineSegment(sketch, "E66.bottom", {"start": v(-36, -3.57) * mm, "end": v(-26, -3.57) * mm});
            skLineSegment(sketch, "E66.top", {"start": v(-36, -13.57) * mm, "end": v(-26, -13.57) * mm});
            skLineSegment(sketch, "E66.left", {"start": v(-36, -3.57) * mm, "end": v(-36, -13.57) * mm});
            skLineSegment(sketch, "E66.right", {"start": v(-26, -3.57) * mm, "end": v(-26, -13.57) * mm});
            skLineSegment(sketch, "E67", {"start": v(-26, -34.57) * mm, "end": v(-26, -13.57) * mm, "construction": true});
            skLineSegment(sketch, "E68", {"start": v(-26, -13.57) * mm, "end": v(-5, -13.57) * mm, "construction": true});
            skLineSegment(sketch, "E69", {"start": v(-5, -34.57) * mm, "end": v(-5, -13.57) * mm, "construction": true});
            skLineSegment(sketch, "E70", {"start": v(-5, -34.57) * mm, "end": v(-26, -34.57) * mm, "construction": true});
            skCircle(sketch, "E71", {"center": v(-31, -8.57) * mm, "radius": 1.5 * mm});
            skLineSegment(sketch, "E72", {"start": v(-36, -13.57) * mm, "end": v(-26, -3.57) * mm, "construction": true});
            skLineSegment(sketch, "E73", {"start": v(-26, -13.57) * mm, "end": v(-36, -3.57) * mm, "construction": true});
            skLineSegment(sketch, "E74", {"start": v(-5, -13.57) * mm, "end": v(5, -3.57) * mm, "construction": true});
            skLineSegment(sketch, "E75", {"start": v(5, -13.57) * mm, "end": v(-5, -3.57) * mm, "construction": true});
            skCircle(sketch, "E76", {"center": v(0, -8.57) * mm, "radius": 1.5 * mm});
            skLineSegment(sketch, "E77", {"start": v(-36, -44.57) * mm, "end": v(-26, -34.57) * mm, "construction": true});
            skLineSegment(sketch, "E78", {"start": v(-26, -44.57) * mm, "end": v(-36, -34.57) * mm, "construction": true});
            skLineSegment(sketch, "E79", {"start": v(-5, -44.57) * mm, "end": v(5, -34.57) * mm, "construction": true});
            skLineSegment(sketch, "E80", {"start": v(5, -44.57) * mm, "end": v(-5, -34.57) * mm, "construction": true});
            skCircle(sketch, "E81", {"center": v(-31, -39.57) * mm, "radius": 1.5 * mm});
            skCircle(sketch, "E82", {"center": v(0, -39.57) * mm, "radius": 1.5 * mm});
            skSolve(sketch);
        }
        {
            var Q0;
            Q0 = qSketchRegion(id + "F31", true);
            extrude(context, id + "F32", {"entities" : qUnion([Q0]), "operationType" : NewBodyOperationType.ADD, "oppositeDirection" : true, "depth" : 8 * mm, "offsetDistance" : 25 * mm});
        }
        {
            var Q0;
            Q0=makeQuery(id+"F13.boolean.opBoolean","INTERSECT",EDGE,{"derivedFrom":[makeQuery(id+"F11.opExtrude","SWEPT_FACE",FACE,{"disambiguationData":[OSD([sQuery(id+"F10.wireOp",EDGE,"E6")])]}),makeQuery(id+"F13.opExtrude","SWEPT_FACE",FACE,{"disambiguationData":[OSD([sQuery(id+"F12.wireOp",EDGE,"E12")])]})]});
            var Q1;
            Q1=makeQuery(id+"F13.boolean.opBoolean","INTERSECT",EDGE,{"derivedFrom":[makeQuery(id+"F11.opExtrude","SWEPT_FACE",FACE,{"disambiguationData":[OSD([sQuery(id+"F10.wireOp",EDGE,"E6")])]}),makeQuery(id+"F13.opExtrude","SWEPT_FACE",FACE,{"disambiguationData":[OSD([sQuery(id+"F12.wireOp",EDGE,"E14")])]})]});
            chamfer(context, id + "F33", {"entities" : qUnion([Q0, Q1]), "width" : 1 * mm, "tangentPropagation" : true});
        }
        {
            var Q0;
            Q0=makeQuery(id+"F24.opExtrude","CAP_EDGE",EDGE,{"disambiguationData":[OSD([sQuery(id+"F23.wireOp",EDGE,"E45.left")])],"isStart":true});
            chamfer(context, id + "F34", {"entities" : qUnion([Q0]), "width" : 2 * mm, "tangentPropagation" : true});
        }
        {
            var Q0;
            Q0=makeQuery(id+"F22.opExtrude","CAP_EDGE",EDGE,{"disambiguationData":[OSD([sQuery(id+"F21.wireOp",EDGE,"E43")])],"isStart":true});
            chamfer(context, id + "F35", {"entities" : qUnion([Q0]), "width" : 2 * mm, "tangentPropagation" : true});
        }
        {
            var Q0;
            Q0=makeQuery(id+"F13.boolean.opBoolean","INTERSECT",EDGE,{"derivedFrom":[makeQuery(id+"F11.opExtrude","SWEPT_FACE",FACE,{"disambiguationData":[OSD([sQuery(id+"F10.wireOp",EDGE,"E4")])]}),makeQuery(id+"F13.opExtrude","SWEPT_FACE",FACE,{"disambiguationData":[OSD([sQuery(id+"F12.wireOp",EDGE,"E14")])]})]});
            chamfer(context, id + "F36", {"entities" : qUnion([Q0]), "width" : 1 * mm, "tangentPropagation" : true});
        }
        {
            var Q0;
            Q0=makeQuery(id+"F19.opExtrude","SWEPT_EDGE",EDGE,{"disambiguationData":[OSD([sQuery(id+"F18.wireOp",EDGE,"E35"),sQuery(id+"F18.wireOp",EDGE,"E36")])]});
            chamfer(context, id + "F37", {"entities" : qUnion([Q0]), "width" : 2 * mm, "tangentPropagation" : true});
        }
        {
            var Q0;
            Q0=makeQuery(id+"F26.opExtrude","CAP_EDGE",EDGE,{"disambiguationData":[OSD([sQuery(id+"F25.wireOp",EDGE,"E48")])],"isStart":false});
            var Q1;
            Q1=makeQuery(id+"F20.boolean.opBoolean","INTERSECT",EDGE,{"derivedFrom":[makeQuery(id+"F19.boolean.opBoolean","MERGE",FACE,{"derivedFrom":[makeQuery(id+"F16.opExtrude","CAP_FACE",FACE,{"disambiguationData":[OSD([sQuery(id+"F15.wireOp",EDGE,"E16"),sQuery(id+"F15.wireOp",EDGE,"E17"),sQuery(id+"F15.wireOp",EDGE,"E18"),sQuery(id+"F15.wireOp",EDGE,"E20"),sQuery(id+"F15.wireOp",EDGE,"E21"),sQuery(id+"F15.wireOp",EDGE,"E22")])],"isStart":false}),makeQuery(id+"F19.opExtrude","SWEPT_FACE",FACE,{"disambiguationData":[OSD([sQuery(id+"F18.wireOp",EDGE,"E39.right")])]})]}),makeQuery(id+"F20.opExtrude","SWEPT_FACE",FACE,{"disambiguationData":[OSD([sQuery(id+"F17.wireOp",EDGE,"E25")])]})]});
            var Q2;
            Q2=makeQuery(id+"F28.boolean.opBoolean","INTERSECT",EDGE,{"derivedFrom":[makeQuery(id+"F26.boolean.opBoolean","MERGE",FACE,{"derivedFrom":[makeQuery(id+"F19.opExtrude","SWEPT_FACE",FACE,{"disambiguationData":[OSD([sQuery(id+"F18.wireOp",EDGE,"E39.left")])]}),makeQuery(id+"F26.opExtrude","CAP_FACE",FACE,{"disambiguationData":[OSD([sQuery(id+"F25.wireOp",EDGE,"E47"),sQuery(id+"F25.wireOp",EDGE,"E48"),sQuery(id+"F25.wireOp",EDGE,"E49"),sQuery(id+"F25.wireOp",EDGE,"E51"),sQuery(id+"F25.wireOp",EDGE,"E52")])],"isStart":false})]}),makeQuery(id+"F28.opExtrude","SWEPT_FACE",FACE,{"disambiguationData":[OSD([sQuery(id+"F27.wireOp",EDGE,"E60")])]})]});
            var Q3;
            Q3=makeQuery(id+"F28.boolean.opBoolean","INTERSECT",EDGE,{"derivedFrom":[makeQuery(id+"F19.boolean.opBoolean","MERGE",FACE,{"derivedFrom":[makeQuery(id+"F16.opExtrude","CAP_FACE",FACE,{"disambiguationData":[OSD([sQuery(id+"F15.wireOp",EDGE,"E16"),sQuery(id+"F15.wireOp",EDGE,"E17"),sQuery(id+"F15.wireOp",EDGE,"E18"),sQuery(id+"F15.wireOp",EDGE,"E20"),sQuery(id+"F15.wireOp",EDGE,"E21"),sQuery(id+"F15.wireOp",EDGE,"E22")])],"isStart":false}),makeQuery(id+"F19.opExtrude","SWEPT_FACE",FACE,{"disambiguationData":[OSD([sQuery(id+"F18.wireOp",EDGE,"E39.right")])]})]}),makeQuery(id+"F28.opExtrude","SWEPT_FACE",FACE,{"disambiguationData":[OSD([sQuery(id+"F27.wireOp",EDGE,"E60")])]})]});
            var Q4;
            Q4=makeQuery(id+"F28.opExtrude","SWEPT_EDGE",EDGE,{"disambiguationData":[OSD([sQuery(id+"F27.wireOp",EDGE,"E55"),sQuery(id+"F27.wireOp",EDGE,"E60")])]});
            var Q5;
            Q5=makeQuery(id+"F30.boolean.opBoolean","INTERSECT",EDGE,{"derivedFrom":[makeQuery(id+"F28.opExtrude","SWEPT_FACE",FACE,{"disambiguationData":[OSD([sQuery(id+"F27.wireOp",EDGE,"E55")])]}),makeQuery(id+"F30.opExtrude","SWEPT_FACE",FACE,{"disambiguationData":[OSD([sQuery(id+"F29.wireOp",EDGE,"E62.right")])]})]});
            var Q6;
            Q6=makeQuery(id+"F30.boolean.opBoolean","INTERSECT",EDGE,{"derivedFrom":[makeQuery(id+"F28.opExtrude","SWEPT_FACE",FACE,{"disambiguationData":[OSD([sQuery(id+"F27.wireOp",EDGE,"E55")])]}),makeQuery(id+"F30.opExtrude","SWEPT_FACE",FACE,{"disambiguationData":[OSD([sQuery(id+"F29.wireOp",EDGE,"E61.right")])]})]});
            var Q7;
            {var subQ0=sQuery(id+"F29.wireOp",EDGE,"E61.right");var subQ1=sQuery(id+"F27.wireOp",EDGE,"E54");var subQ2=makeQuery(id+"F29.imprint","INTERSECT",VERTEX,{"derivedFrom":[makeQuery(id+"F28.opExtrude","SWEPT_EDGE",EDGE,{"disambiguationData":[OSD([subQ1,sQuery(id+"F27.wireOp",EDGE,"E55")])]}),subQ0]});Q7=makeQuery(id+"F30.opExtrude","TWEAK_EDGE",EDGE,{"derivedFrom":[makeQuery(id+"F26.boolean.opBoolean","MERGE",FACE,{"derivedFrom":[makeQuery(id+"F19.boolean.opBoolean","MERGE",FACE,{"derivedFrom":[makeQuery(id+"F16.opExtrude","SWEPT_FACE",FACE,{"disambiguationData":[OSD([sQuery(id+"F15.wireOp",EDGE,"E17")])]}),makeQuery(id+"F19.opExtrude","SWEPT_FACE",FACE,{"disambiguationData":[OSD([sQuery(id+"F18.wireOp",EDGE,"E37")])]})]}),makeQuery(id+"F26.opExtrude","SWEPT_FACE",FACE,{"disambiguationData":[OSD([sQuery(id+"F25.wireOp",EDGE,"E52")])]})]}),makeQuery(id+"F29.imprint","IMPRINT",EDGE,{"disambiguationData":[TD([[subQ2,1.0]])],"derivedFrom":subQ0}),makeQuery(id+"F29.imprint","IMPRINT",EDGE,{"disambiguationData":[TD([[makeQuery(id+"F29.imprint","INTERSECT",VERTEX,{"derivedFrom":[sQuery(id+"F29.wireOp",EDGE,"E61.top"),subQ0]}),1.0]])],"derivedFrom":subQ0})]});}
            var Q8;
            {var subQ0=sQuery(id+"F29.wireOp",EDGE,"E62.right");var subQ1=sQuery(id+"F27.wireOp",EDGE,"E54");var subQ2=makeQuery(id+"F29.imprint","INTERSECT",VERTEX,{"derivedFrom":[makeQuery(id+"F28.opExtrude","SWEPT_EDGE",EDGE,{"disambiguationData":[OSD([subQ1,sQuery(id+"F27.wireOp",EDGE,"E55")])]}),subQ0]});Q8=makeQuery(id+"F30.opExtrude","TWEAK_EDGE",EDGE,{"derivedFrom":[makeQuery(id+"F26.boolean.opBoolean","MERGE",FACE,{"derivedFrom":[makeQuery(id+"F19.boolean.opBoolean","MERGE",FACE,{"derivedFrom":[makeQuery(id+"F16.opExtrude","SWEPT_FACE",FACE,{"disambiguationData":[OSD([sQuery(id+"F15.wireOp",EDGE,"E17")])]}),makeQuery(id+"F19.opExtrude","SWEPT_FACE",FACE,{"disambiguationData":[OSD([sQuery(id+"F18.wireOp",EDGE,"E37")])]})]}),makeQuery(id+"F26.opExtrude","SWEPT_FACE",FACE,{"disambiguationData":[OSD([sQuery(id+"F25.wireOp",EDGE,"E52")])]})]}),makeQuery(id+"F29.imprint","IMPRINT",EDGE,{"disambiguationData":[TD([[subQ2,1.0]])],"derivedFrom":subQ0}),makeQuery(id+"F29.imprint","IMPRINT",EDGE,{"disambiguationData":[TD([[makeQuery(id+"F29.imprint","INTERSECT",VERTEX,{"derivedFrom":[sQuery(id+"F29.wireOp",EDGE,"E62.top"),subQ0]}),1.0]])],"derivedFrom":subQ0})]});}
            chamfer(context, id + "F38", {"entities" : qUnion([Q0, Q1, Q2, Q3, Q4, Q5, Q6, Q7, Q8]), "width" : 2 * mm, "tangentPropagation" : true});
        }
        {
            var Q0;
            Q0=makeQuery(id+"F32.opExtrude","SWEPT_EDGE",EDGE,{"disambiguationData":[OSD([sQuery(id+"F31.wireOp",EDGE,"E64.top"),sQuery(id+"F31.wireOp",EDGE,"E64.right")])]});
            var Q1;
            Q1=makeQuery(id+"F32.opExtrude","SWEPT_EDGE",EDGE,{"disambiguationData":[OSD([sQuery(id+"F31.wireOp",EDGE,"E66.top"),sQuery(id+"F31.wireOp",EDGE,"E66.right")])]});
            var Q2;
            Q2=makeQuery(id+"F32.opExtrude","SWEPT_EDGE",EDGE,{"disambiguationData":[OSD([sQuery(id+"F31.wireOp",EDGE,"E65.top"),sQuery(id+"F31.wireOp",EDGE,"E65.right")])]});
            var Q3;
            Q3=makeQuery(id+"F32.opExtrude","SWEPT_EDGE",EDGE,{"disambiguationData":[OSD([sQuery(id+"F31.wireOp",EDGE,"E63.top"),sQuery(id+"F31.wireOp",EDGE,"E63.right")])]});
            chamfer(context, id + "F39", {"entities" : qUnion([Q0, Q1, Q2, Q3]), "width" : 5 * mm, "tangentPropagation" : true});
        }
    });
